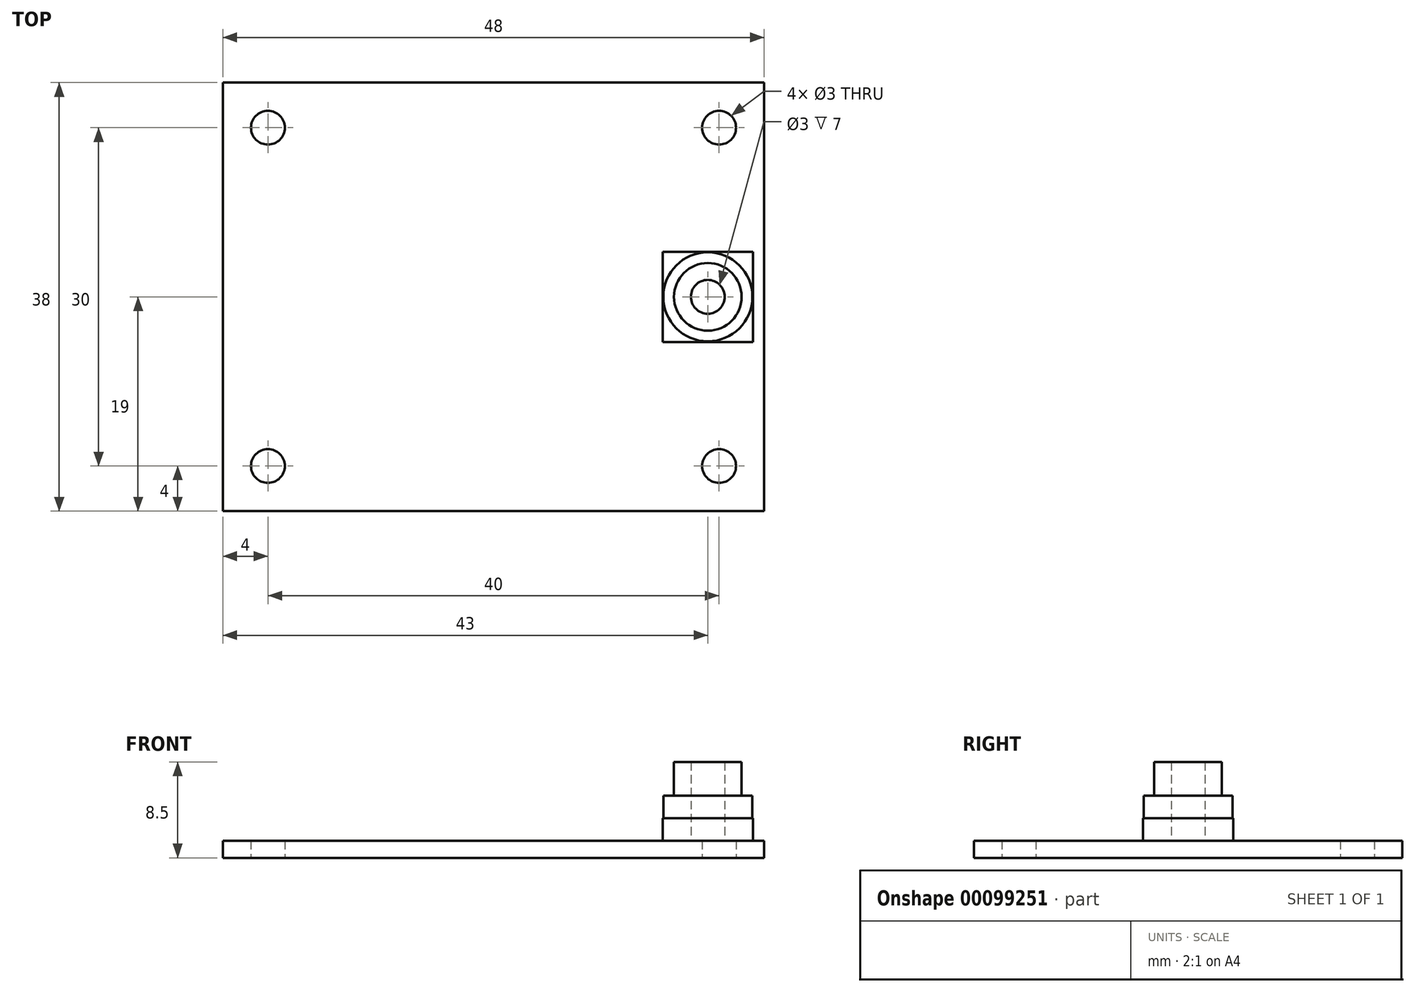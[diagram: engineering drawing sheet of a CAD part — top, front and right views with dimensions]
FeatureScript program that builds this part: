
annotation { "Feature Type Name" : "Feature", "Feature Type Description" : "" }
export const myFeature = defineFeature(function(context is Context, id is Id, definition is map)
    precondition{}
    {
        {
            var Q0;
            Q0=qCreatedBy(makeId("Top.planeOp"),FACE);
            var sketch = newSketch(context, id + "F0", { "sketchPlane" : qUnion([Q0])});
            skLineSegment(sketch, "E0.bottom", {"start": v(0, 0) * mm, "end": v(48, 0) * mm});
            skLineSegment(sketch, "E0.top", {"start": v(0, 38) * mm, "end": v(48, 38) * mm});
            skLineSegment(sketch, "E0.left", {"start": v(0, 0) * mm, "end": v(0, 38) * mm});
            skLineSegment(sketch, "E0.right", {"start": v(48, 0) * mm, "end": v(48, 38) * mm});
            skCircle(sketch, "E1", {"center": v(4, 4) * mm, "radius": 1.5 * mm});
            skCircle(sketch, "E2.0.1.0", {"center": v(4, 34) * mm, "radius": 1.5 * mm});
            skCircle(sketch, "E2.1.0.0", {"center": v(44, 4) * mm, "radius": 1.5 * mm});
            skCircle(sketch, "E2.1.1.0", {"center": v(44, 34) * mm, "radius": 1.5 * mm});
            skLineSegment(sketch, "E2.direction1", {"start": v(4, 4) * mm, "end": v(44, 4) * mm, "construction": true});
            skLineSegment(sketch, "E2.direction2", {"start": v(4, 4) * mm, "end": v(4, 34) * mm, "construction": true});
            skSolve(sketch);
        }
        {
            var Q0;
            Q0 = qSketchRegion(id + "F0", true);
            var Q1;
            Q1=makeQuery(id+"F0.imprint","IMPRINT",FACE,{"disambiguationData":[TD([[makeQuery(id+"F0.imprint","IMPRINT",EDGE,{"derivedFrom":sQuery(id+"F0.wireOp",EDGE,"E0.bottom")}),1.0]])]});
            extrude(context, id + "F1", {"entities" : qUnion([Q0, Q1]), "depth" : 1.5 * mm});
        }
        {
            var Q0;
            Q0=makeQuery(id+"F1.opExtrude","CAP_FACE",FACE,{"disambiguationData":[OSD([sQuery(id+"F0.wireOp",EDGE,"E0.bottom"),sQuery(id+"F0.wireOp",EDGE,"E0.top"),sQuery(id+"F0.wireOp",EDGE,"E0.left"),sQuery(id+"F0.wireOp",EDGE,"E0.right"),sQuery(id+"F0.wireOp",EDGE,"E1"),sQuery(id+"F0.wireOp",EDGE,"E2.0.1.0"),sQuery(id+"F0.wireOp",EDGE,"E2.1.0.0"),sQuery(id+"F0.wireOp",EDGE,"E2.1.1.0")])],"isStart":false});
            var sketch = newSketch(context, id + "F2", { "sketchPlane" : qUnion([Q0])});
            skLineSegment(sketch, "E3", {"start": v(48, 19) * mm, "end": v(47, 19) * mm});
            skPoint(sketch, "E3.endSnap0", {"position": v(48, 19) * mm});
            skLineSegment(sketch, "E4", {"start": v(47, 19) * mm, "end": v(47, 23) * mm, "construction": true});
            skLineSegment(sketch, "E5.bottom", {"start": v(47, 23) * mm, "end": v(39, 23) * mm});
            skLineSegment(sketch, "E5.top", {"start": v(47, 15) * mm, "end": v(39, 15) * mm});
            skLineSegment(sketch, "E5.left", {"start": v(47, 23) * mm, "end": v(47, 15) * mm});
            skLineSegment(sketch, "E5.right", {"start": v(39, 23) * mm, "end": v(39, 15) * mm});
            skCircle(sketch, "E6", {"center": v(43, 19) * mm, "radius": 3.95 * mm});
            skCircle(sketch, "E7", {"center": v(43, 19) * mm, "radius": 3 * mm});
            skCircle(sketch, "E8", {"center": v(43, 19) * mm, "radius": 1.5 * mm});
            skSolve(sketch);
        }
        {
            var Q0;
            {var subQ3=sQuery(id+"F2.wireOp",EDGE,"E5.bottom");Q0=makeQuery(id+"F2.imprint","IMPRINT",FACE,{"disambiguationData":[TD([[makeQuery(id+"F2.imprint","IMPRINT",EDGE,{"derivedFrom":subQ3}),1.0]])]});}
            extrude(context, id + "F3", {"entities" : qUnion([Q0]), "depth" : 2 * mm});
        }
        {
            var Q0;
            Q0=makeQuery(id+"F2.imprint","IMPRINT",FACE,{"disambiguationData":[TD([[makeQuery(id+"F2.imprint","IMPRINT",EDGE,{"derivedFrom":sQuery(id+"F2.wireOp",EDGE,"E6")}),1.0]])]});
            extrude(context, id + "F4", {"entities" : qUnion([Q0]), "operationType" : NewBodyOperationType.ADD, "depth" : 4 * mm});
        }
        {
            var Q0;
            Q0=makeQuery(id+"F2.imprint","IMPRINT",FACE,{"disambiguationData":[TD([[makeQuery(id+"F2.imprint","IMPRINT",EDGE,{"derivedFrom":sQuery(id+"F2.wireOp",EDGE,"E7")}),1.0]])]});
            extrude(context, id + "F5", {"entities" : qUnion([Q0]), "operationType" : NewBodyOperationType.ADD, "depth" : 7 * mm});
        }
    });
